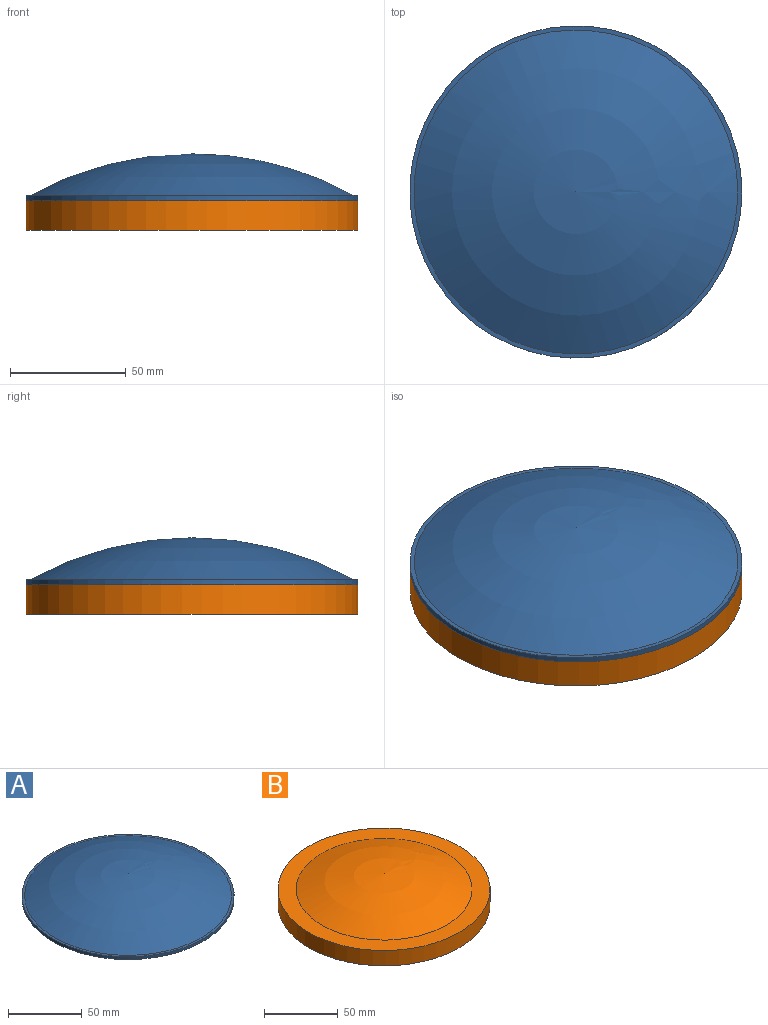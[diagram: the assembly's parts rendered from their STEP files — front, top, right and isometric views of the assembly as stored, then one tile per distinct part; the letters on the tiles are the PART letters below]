
ASSEMBLY  parts=2 mates=1
PART A: 5 faces, bbox 143.5x143.5x20.3 mm
  f0: sphere r=144.78mm, area 11652.3mm2, adj f1
  f1: plane 143.51x143.51mm, normal (0,0,-1), area 5038.5mm2, adj f0,f2
  f2: cylinder r=71.75mm len=143.51mm, axis (0,0,1), area 1030.6mm2, adj f1,f3
  f3: plane 143.51x143.51mm, normal (0,0,1), area 791.7mm2, adj f2,f4
  f4: sphere r=144.78mm, area 16405.5mm2, adj f3
PART B: 4 faces, bbox 143.5x143.5x25.5 mm
  f0: cylinder r=71.75mm len=143.51mm, axis (0,0,1), area 5725.8mm2, adj f1,f3
  f1: plane 143.51x143.51mm, normal (0,0,-1), area 16175.4mm2, adj f0
  f2: sphere r=144.78mm, area 11647.7mm2, adj f3
  f3: plane 143.51x143.51mm, normal (0,0,1), area 5042.8mm2, adj f0,f2
PLACE A t=(0.83,-0.63,-1.78)mm
PLACE B t=(0.83,-0.63,-1.78)mm
MATE fastened A.f2 <-> B.f0  axis (0,0,-1) through (0.83,-0.63,-1.78)mm
